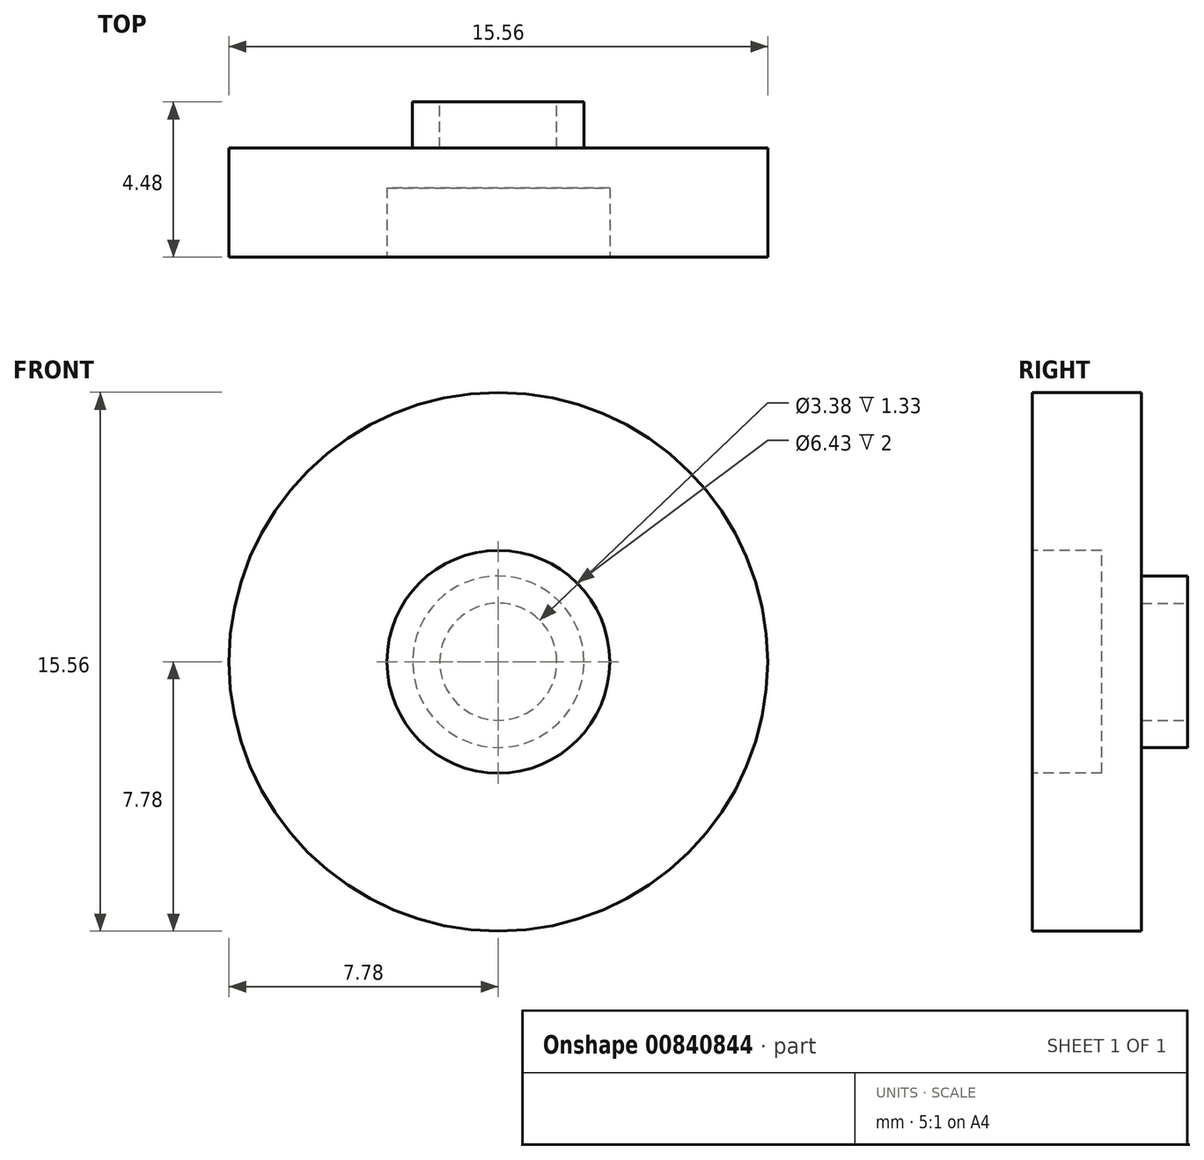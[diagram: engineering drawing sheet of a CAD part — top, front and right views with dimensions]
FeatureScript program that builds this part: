
annotation { "Feature Type Name" : "Feature", "Feature Type Description" : "" }
export const myFeature = defineFeature(function(context is Context, id is Id, definition is map)
    precondition{}
    {
        {
            var Q0;
            Q0=qCreatedBy(makeId("Front.planeOp"),FACE);
            var sketch = newSketch(context, id + "F0", { "sketchPlane" : qUnion([Q0])});
            skCircle(sketch, "E0", {"center": v(0, 0) * mm, "radius": 2.48 * mm});
            skCircle(sketch, "E1", {"center": v(0, 0) * mm, "radius": 1.69 * mm});
            skSolve(sketch);
        }
        {
            var Q0;
            Q0=makeQuery(id+"F0.imprint","IMPRINT",FACE,{"disambiguationData":[TD([[makeQuery(id+"F0.imprint","IMPRINT",EDGE,{"derivedFrom":sQuery(id+"F0.wireOp",EDGE,"E0")}),1.0]])]});
            extrude(context, id + "F1", {"entities" : qUnion([Q0]), "depth" : 1.33 * mm, "offsetDistance" : 25 * mm});
        }
        {
            var Q0;
            Q0=makeQuery(id+"F1.opExtrude","CAP_FACE",FACE,{"disambiguationData":[OSD([sQuery(id+"F0.wireOp",EDGE,"E0"),sQuery(id+"F0.wireOp",EDGE,"E1")])],"isStart":false});
            var sketch = newSketch(context, id + "F2", { "sketchPlane" : qUnion([Q0])});
            skCircle(sketch, "E2", {"center": v(0, 0) * mm, "radius": 7.78 * mm});
            skSolve(sketch);
        }
        {
            var Q0;
            Q0=qSketchRegion(id+"F2",true);
            extrude(context, id + "F3", {"entities" : qUnion([Q0]), "operationType" : NewBodyOperationType.ADD, "depth" : 3.15 * mm, "offsetDistance" : 25 * mm});
        }
        {
            var Q0;
            Q0=makeQuery(id+"F3.opExtrude","CAP_FACE",FACE,{"disambiguationData":[OSD([sQuery(id+"F2.wireOp",EDGE,"E2")])],"isStart":false});
            var sketch = newSketch(context, id + "F4", { "sketchPlane" : qUnion([Q0])});
            skCircle(sketch, "E3", {"center": v(0, 0) * mm, "radius": 3.21 * mm});
            skSolve(sketch);
        }
        {
            var Q0;
            Q0=qSketchRegion(id+"F4",true);
            extrude(context, id + "F5", {"entities" : qUnion([Q0]), "operationType" : NewBodyOperationType.REMOVE, "oppositeDirection" : true, "depth" : 2 * mm, "offsetDistance" : 25 * mm});
        }
    });
